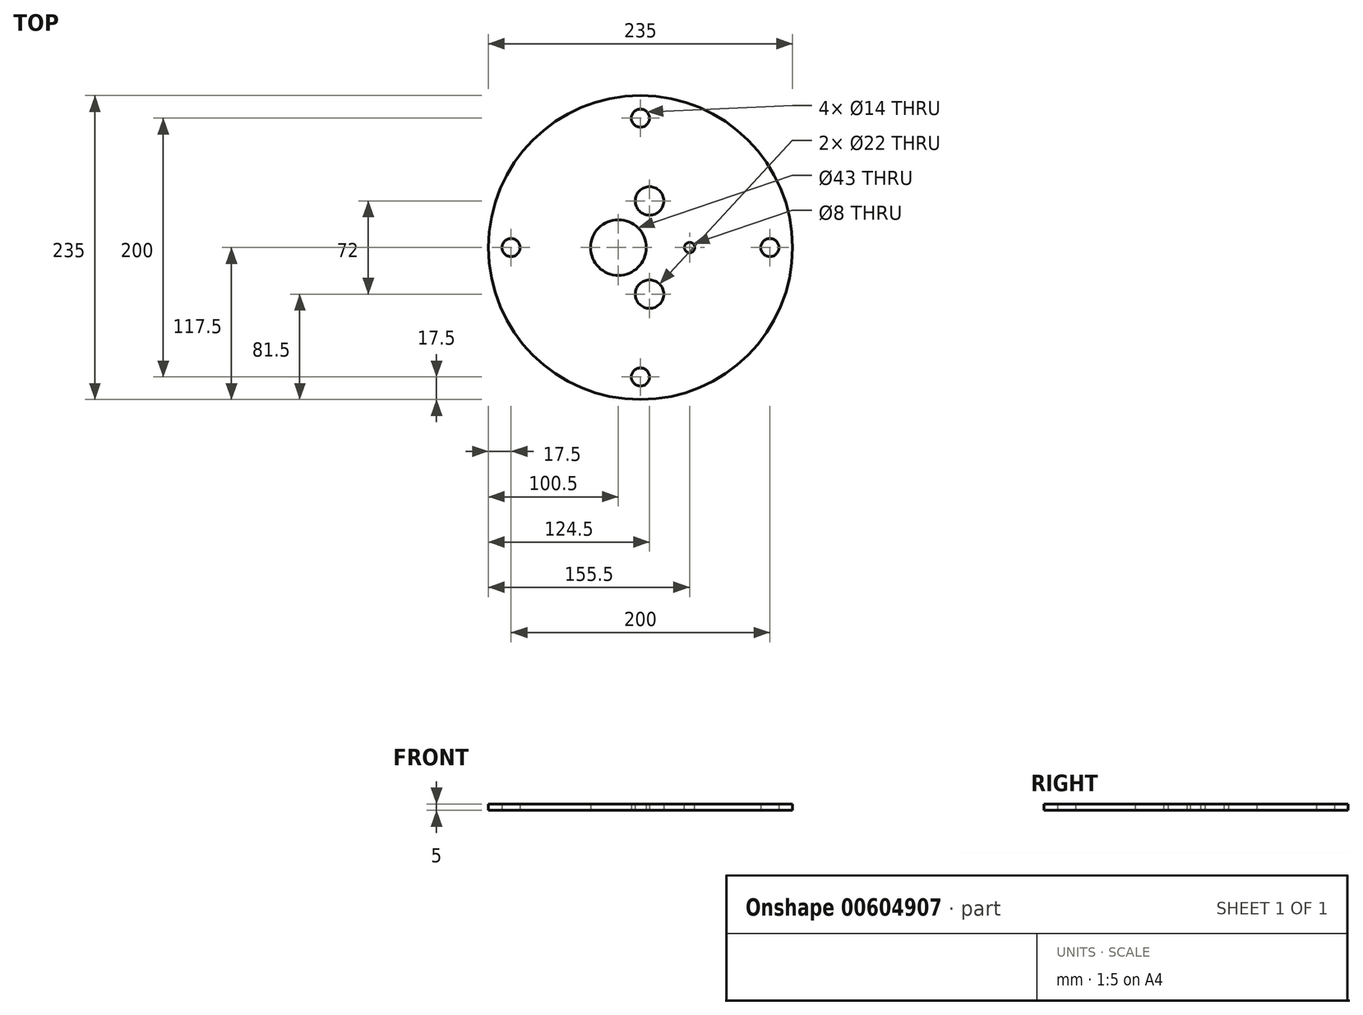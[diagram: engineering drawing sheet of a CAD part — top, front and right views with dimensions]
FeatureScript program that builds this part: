
annotation { "Feature Type Name" : "Feature", "Feature Type Description" : "" }
export const myFeature = defineFeature(function(context is Context, id is Id, definition is map)
    precondition{}
    {
        {
            var Q0;
            Q0=qCreatedBy(makeId("Top.planeOp"),FACE);
            var sketch = newSketch(context, id + "F0", { "sketchPlane" : qUnion([Q0])});
            skLineSegment(sketch, "E0", {"start": v(-63.5, 0) * mm, "end": v(117.5, 0) * mm, "construction": true});
            skCircle(sketch, "E1", {"center": v(0, 0) * mm, "radius": 117.5 * mm});
            skCircle(sketch, "E2", {"center": v(0, 0) * mm, "radius": 55 * mm, "construction": true});
            skLineSegment(sketch, "E3", {"start": v(0, 0) * mm, "end": v(0, -73.71) * mm, "construction": true});
            skCircle(sketch, "E4", {"center": v(7, -36) * mm, "radius": 11 * mm});
            skCircle(sketch, "E5", {"center": v(0, 0) * mm, "radius": 85 * mm, "construction": true});
            skLineSegment(sketch, "E6", {"start": v(0, 0) * mm, "end": v(0, 72) * mm, "construction": true});
            skCircle(sketch, "E7", {"center": v(7, 36) * mm, "radius": 11 * mm});
            skCircle(sketch, "E8", {"center": v(-17, 0) * mm, "radius": 21.5 * mm});
            skCircle(sketch, "E9", {"center": v(7, -36) * mm, "radius": 16 * mm, "construction": true});
            skCircle(sketch, "E10", {"center": v(7, 36) * mm, "radius": 16 * mm, "construction": true});
            skPoint(sketch, "E11", {"position": v(0, 36) * mm});
            skSolve(sketch);
        }
        {
            var Q0;
            Q0=qSketchRegion(id+"F0",true);
            extrude(context, id + "F1", {"entities" : qUnion([Q0]), "depth" : 5 * mm, "offsetDistance" : 25 * mm});
        }
        {
            var Q0;
            Q0=makeQuery(id+"F1.opExtrude","CAP_FACE",FACE,{"disambiguationData":[OSD([sQuery(id+"F0.wireOp",EDGE,"E1")])],"isStart":true});
            var sketch = newSketch(context, id + "F2", { "sketchPlane" : qUnion([Q0])});
            skCircle(sketch, "E12", {"center": v(0, 0) * mm, "radius": 100 * mm, "construction": true});
            skLineSegment(sketch, "E13", {"start": v(-100, 0) * mm, "end": v(100, 0) * mm, "construction": true});
            skLineSegment(sketch, "E14", {"start": v(0, 100) * mm, "end": v(0, -100) * mm, "construction": true});
            skCircle(sketch, "E15", {"center": v(-100, 0) * mm, "radius": 7 * mm});
            skCircle(sketch, "E16", {"center": v(0, 100) * mm, "radius": 7 * mm});
            skCircle(sketch, "E17", {"center": v(100, 0) * mm, "radius": 7 * mm});
            skCircle(sketch, "E18", {"center": v(0, -100) * mm, "radius": 7 * mm});
            skSolve(sketch);
        }
        {
            var Q0;
            Q0=qSketchRegion(id+"F2",true);
            extrude(context, id + "F3", {"entities" : qUnion([Q0]), "operationType" : NewBodyOperationType.REMOVE, "endBound" : BoundingType.THROUGH_ALL, "oppositeDirection" : true, "depth" : 25 * mm, "offsetDistance" : 25 * mm});
        }
        {
            var Q0;
            Q0=makeQuery(id+"F1.opExtrude","CAP_FACE",FACE,{"disambiguationData":[OSD([sQuery(id+"F0.wireOp",EDGE,"E1"),sQuery(id+"F0.wireOp",EDGE,"E4"),sQuery(id+"F0.wireOp",EDGE,"E7"),sQuery(id+"F0.wireOp",EDGE,"JtC9ZSA9-kQVS-lnJV-iCpg-UXejyJ5aiTIN"),sQuery(id+"F0.wireOp",EDGE,"E8")])],"isStart":false});
            var sketch = newSketch(context, id + "F4", { "sketchPlane" : qUnion([Q0])});
            skLineSegment(sketch, "E19", {"start": v(0, 0) * mm, "end": v(0, 54.39) * mm, "construction": true});
            skCircle(sketch, "E20.MirrorC", {"center": v(38, 0) * mm, "radius": 4 * mm});
            skLineSegment(sketch, "E21", {"start": v(0, 0) * mm, "end": v(38, 0) * mm, "construction": true});
            skSolve(sketch);
        }
        {
            var Q0;
            Q0=qSketchRegion(id+"F4",true);
            extrude(context, id + "F5", {"entities" : qUnion([Q0]), "operationType" : NewBodyOperationType.REMOVE, "endBound" : BoundingType.THROUGH_ALL, "oppositeDirection" : true, "depth" : 25 * mm, "offsetDistance" : 25 * mm});
        }
    });
